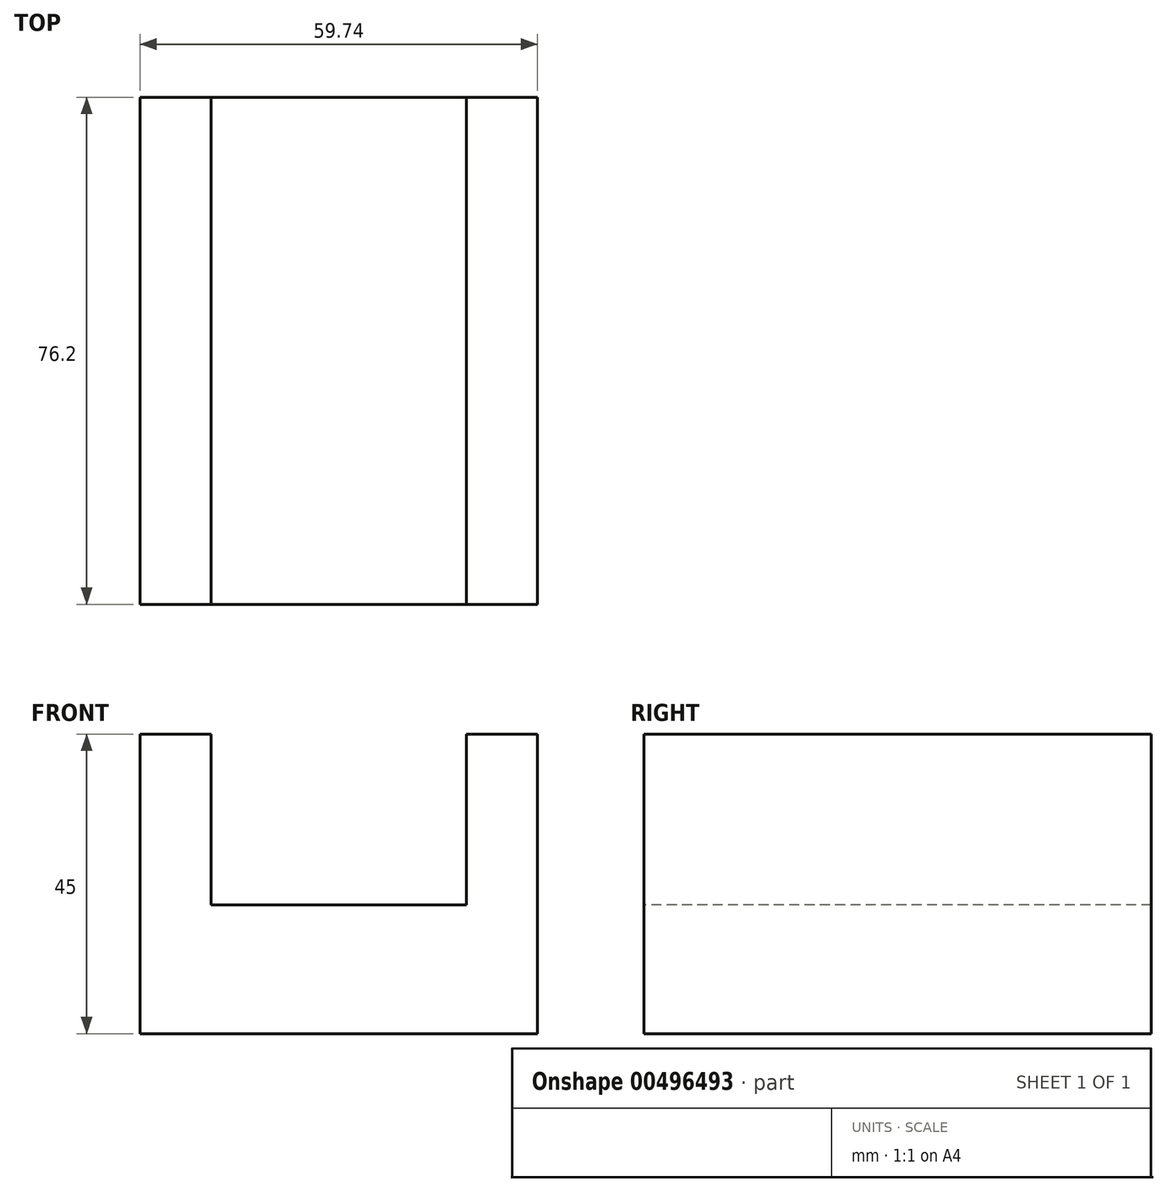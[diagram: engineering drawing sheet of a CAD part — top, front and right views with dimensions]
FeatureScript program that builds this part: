
annotation { "Feature Type Name" : "Feature", "Feature Type Description" : "" }
export const myFeature = defineFeature(function(context is Context, id is Id, definition is map)
    precondition{}
    {
        {
            var Q0;
            Q0=qCreatedBy(makeId("Front.planeOp"),FACE);
            var sketch = newSketch(context, id + "F0", { "sketchPlane" : qUnion([Q0])});
            skLineSegment(sketch, "E0.bottom", {"start": v(0, 0) * mm, "end": v(59.74, 0) * mm});
            skLineSegment(sketch, "E0.top", {"start": v(0, 45) * mm, "end": v(10.67, 45) * mm});
            skLineSegment(sketch, "E0.left", {"start": v(0, 0) * mm, "end": v(0, 45) * mm});
            skLineSegment(sketch, "E0.right", {"start": v(59.74, 0) * mm, "end": v(59.74, 45) * mm});
            skLineSegment(sketch, "E1.top", {"start": v(10.67, 19.35) * mm, "end": v(49.07, 19.35) * mm});
            skLineSegment(sketch, "E1.left", {"start": v(10.67, 45) * mm, "end": v(10.67, 19.35) * mm});
            skLineSegment(sketch, "E1.right", {"start": v(49.07, 45) * mm, "end": v(49.07, 19.35) * mm});
            skLineSegment(sketch, "E2.trimOffspring", {"start": v(49.07, 45) * mm, "end": v(59.74, 45) * mm});
            skSolve(sketch);
        }
        {
            var Q0;
            Q0=makeQuery(id+"F0.imprint","IMPRINT",FACE,{"disambiguationData":[TD([[makeQuery(id+"F0.imprint","IMPRINT",EDGE,{"derivedFrom":sQuery(id+"F0.wireOp",EDGE,"E0.bottom")}),1.0]])]});
            extrude(context, id + "F1", {"entities" : qUnion([Q0]), "oppositeDirection" : true, "depth" : 76.2 * mm});
        }
    });
